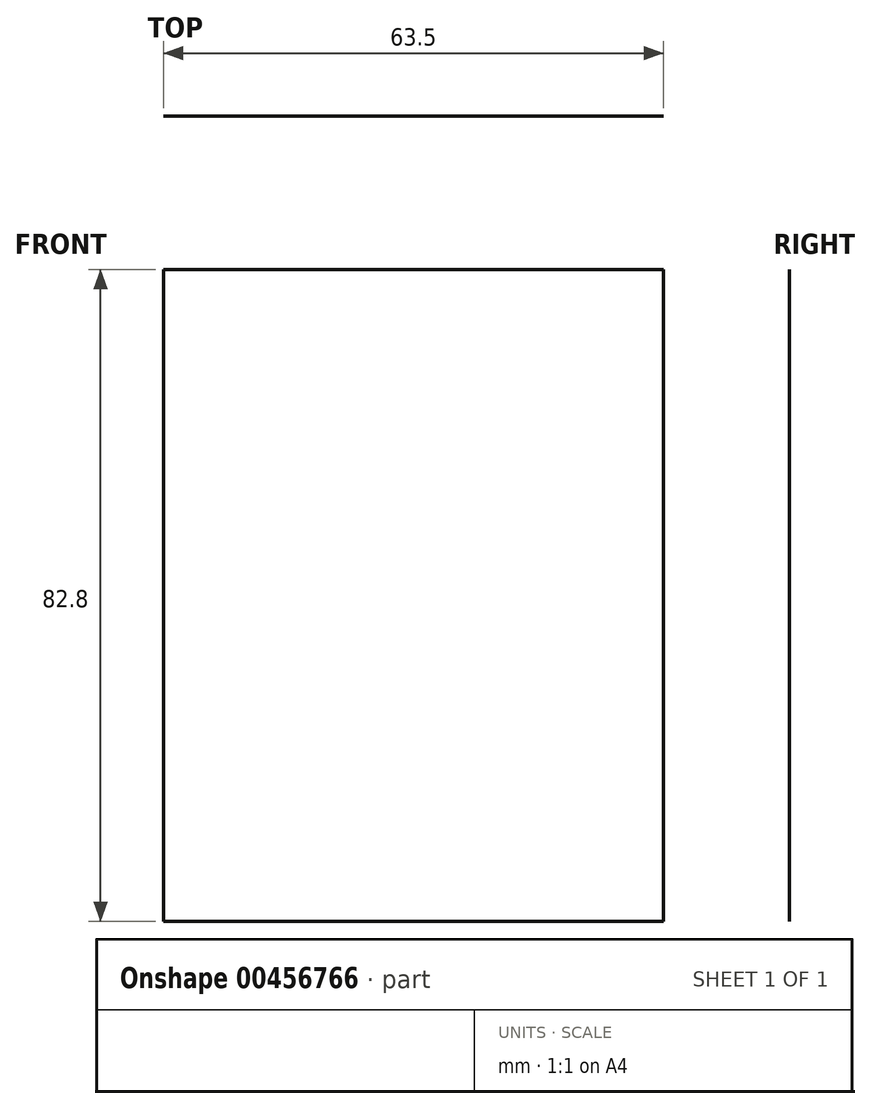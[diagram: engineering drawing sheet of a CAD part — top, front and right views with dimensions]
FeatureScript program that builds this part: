
annotation { "Feature Type Name" : "Feature", "Feature Type Description" : "" }
export const myFeature = defineFeature(function(context is Context, id is Id, definition is map)
    precondition{}
    {
        {
            var Q0;
            Q0=qCreatedBy(makeId("Front.planeOp"),FACE);
            var sketch = newSketch(context, id + "F0", { "sketchPlane" : qUnion([Q0])});
            skLineSegment(sketch, "E0.bottom", {"start": v(-31.75, 41.4) * mm, "end": v(31.75, 41.4) * mm});
            skLineSegment(sketch, "E0.top", {"start": v(-31.75, -41.4) * mm, "end": v(31.75, -41.4) * mm});
            skLineSegment(sketch, "E0.left", {"start": v(-31.75, 41.4) * mm, "end": v(-31.75, -41.4) * mm});
            skLineSegment(sketch, "E0.right", {"start": v(31.75, 41.4) * mm, "end": v(31.75, -41.4) * mm});
            skPoint(sketch, "E0.middle", {"position": v(0, 0) * mm});
            skSolve(sketch);
        }
        {
            var Q0;
            Q0=makeQuery(id+"F0.imprint","IMPRINT",FACE,{"disambiguationData":[TD([[makeQuery(id+"F0.imprint","IMPRINT",EDGE,{"derivedFrom":sQuery(id+"F0.wireOp",EDGE,"E0.bottom")}),-1.0]])]});
            extrude(context, id + "F1", {"entities" : qUnion([Q0]), "depth" : 1 / 203.2 * mm});
        }
    });
